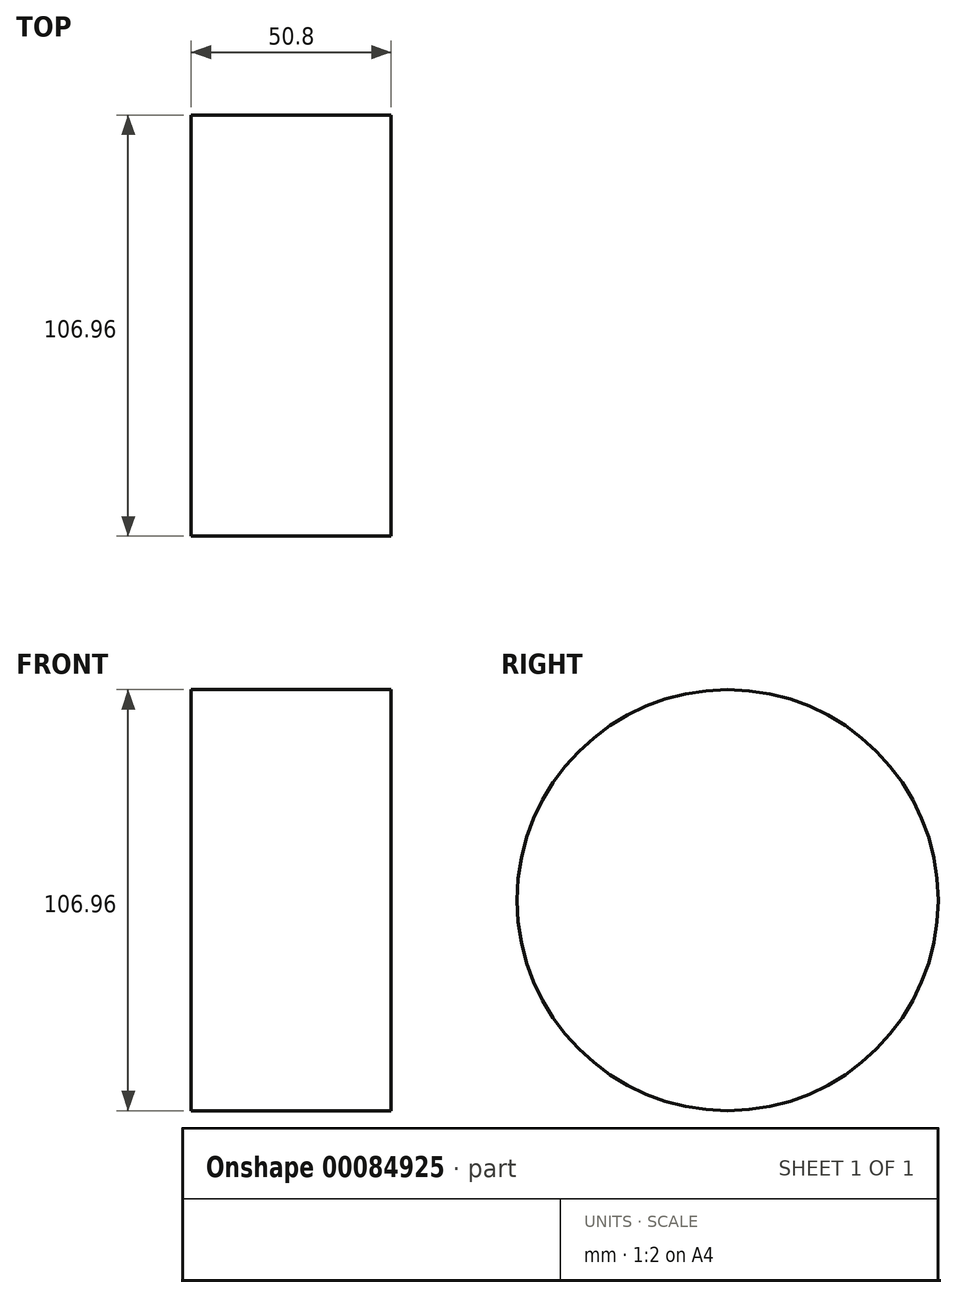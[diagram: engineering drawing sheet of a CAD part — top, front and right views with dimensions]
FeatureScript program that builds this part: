
annotation { "Feature Type Name" : "Feature", "Feature Type Description" : "" }
export const myFeature = defineFeature(function(context is Context, id is Id, definition is map)
    precondition{}
    {
        {
            var Q0;
            Q0=qCreatedBy(makeId("Right.planeOp"),FACE);
            var sketch = newSketch(context, id + "F0", { "sketchPlane" : qUnion([Q0])});
            skCircle(sketch, "E0", {"center": v(0, 0) * mm, "radius": 53.48 * mm});
            skSolve(sketch);
        }
        {
            var Q0;
            Q0 = qSketchRegion(id + "F0", true);
            var Q1;
            Q1=makeQuery(id+"F0.imprint","IMPRINT",FACE,{"disambiguationData":[TD([[makeQuery(id+"F0.imprint","IMPRINT",EDGE,{"derivedFrom":sQuery(id+"F0.wireOp",EDGE,"E0")}),1.0]])]});
            extrude(context, id + "F1", {"entities" : qUnion([Q0, Q1]), "depth" : 50.8 * mm});
        }
    });
